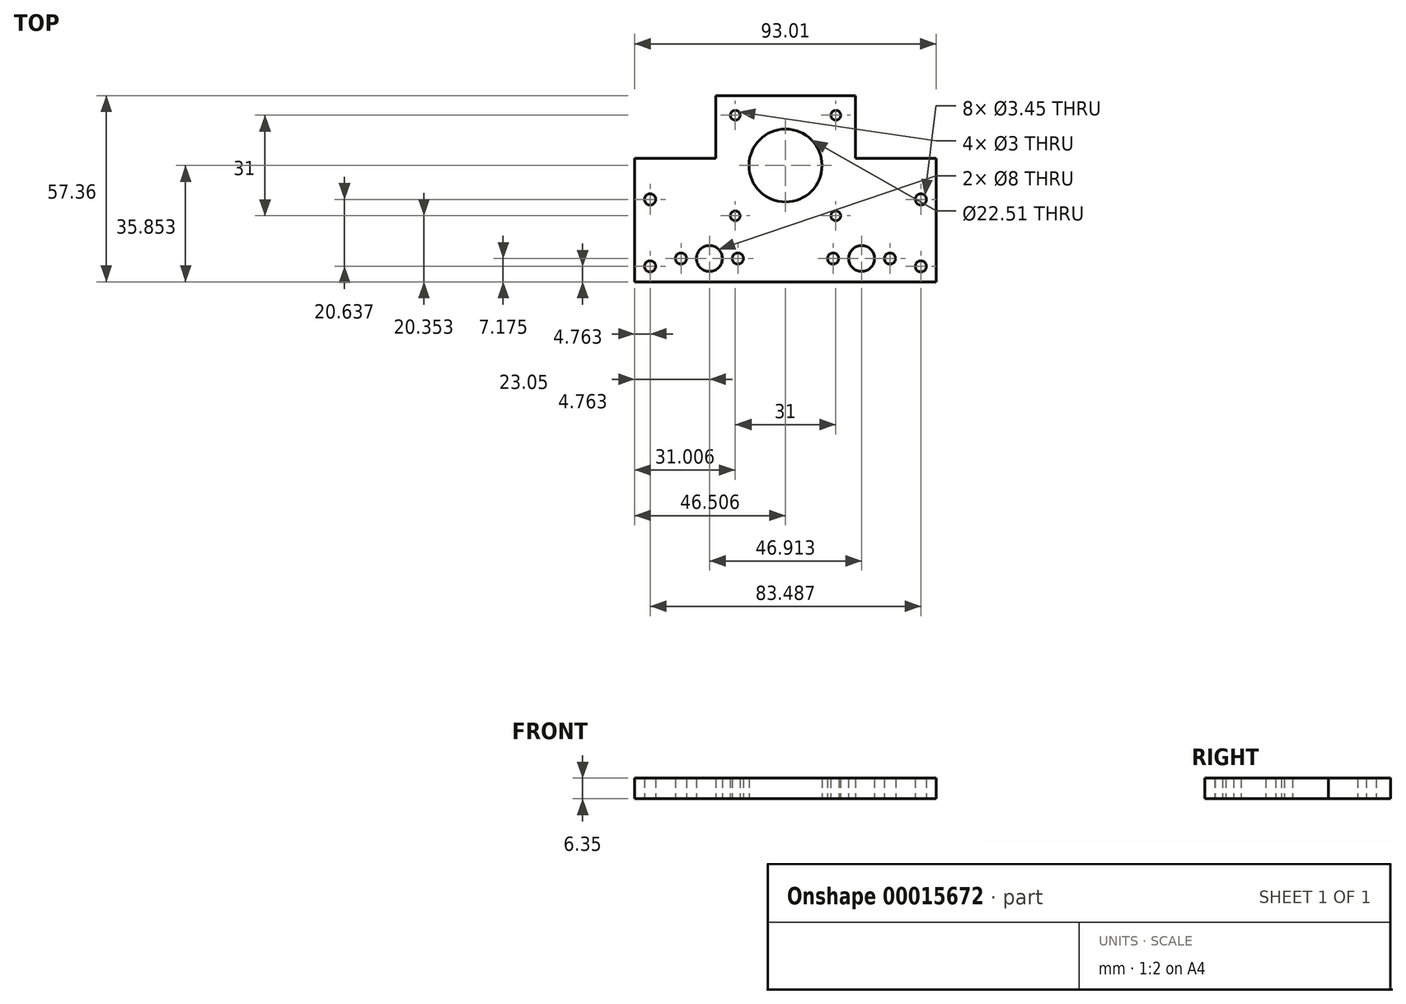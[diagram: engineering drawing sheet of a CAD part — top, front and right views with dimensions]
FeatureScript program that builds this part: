
annotation { "Feature Type Name" : "Feature", "Feature Type Description" : "" }
export const myFeature = defineFeature(function(context is Context, id is Id, definition is map)
    precondition{}
    {
        {
            var Q0;
            Q0=qCreatedBy(makeId("Top.planeOp"),FACE);
            var sketch = newSketch(context, id + "F0", { "sketchPlane" : qUnion([Q0])});
            skLineSegment(sketch, "E0.top", {"start": v(0, -38.1) * mm, "end": v(93.01, -38.1) * mm});
            skLineSegment(sketch, "E0.left", {"start": v(0, 0) * mm, "end": v(0, -38.1) * mm});
            skLineSegment(sketch, "E0.right", {"start": v(93.01, 0) * mm, "end": v(93.01, -38.1) * mm});
            skLineSegment(sketch, "E1", {"start": v(23.05, 0) * mm, "end": v(23.05, -30.92) * mm, "construction": true});
            skLineSegment(sketch, "E2", {"start": v(69.96, 0) * mm, "end": v(69.96, -30.92) * mm, "construction": true});
            skLineSegment(sketch, "E3", {"start": v(61.2, -30.92) * mm, "end": v(78.73, -30.92) * mm, "construction": true});
            skLineSegment(sketch, "E4", {"start": v(14.29, -30.92) * mm, "end": v(31.81, -30.92) * mm, "construction": true});
            skCircle(sketch, "E5", {"center": v(14.29, -30.92) * mm, "radius": 1.73 * mm});
            skCircle(sketch, "E6", {"center": v(23.05, -30.92) * mm, "radius": 4 * mm});
            skCircle(sketch, "E7", {"center": v(31.81, -30.92) * mm, "radius": 1.73 * mm});
            skCircle(sketch, "E8", {"center": v(61.2, -30.92) * mm, "radius": 1.73 * mm});
            skCircle(sketch, "E9", {"center": v(78.73, -30.92) * mm, "radius": 1.73 * mm});
            skCircle(sketch, "E10", {"center": v(69.96, -30.92) * mm, "radius": 4 * mm});
            skLineSegment(sketch, "E11", {"start": v(23.05, -30.92) * mm, "end": v(23.05, -38.1) * mm});
            skLineSegment(sketch, "E12", {"start": v(88.25, 0) * mm, "end": v(88.25, -12.7) * mm, "construction": true});
            skLineSegment(sketch, "E13", {"start": v(88.25, -12.7) * mm, "end": v(88.25, -33.34) * mm, "construction": true});
            skLineSegment(sketch, "E14", {"start": v(4.76, -33.34) * mm, "end": v(4.76, -12.7) * mm, "construction": true});
            skLineSegment(sketch, "E15", {"start": v(4.76, -12.7) * mm, "end": v(4.76, 0) * mm, "construction": true});
            skCircle(sketch, "E16", {"center": v(88.25, -33.34) * mm, "radius": 1.73 * mm});
            skCircle(sketch, "E17", {"center": v(88.25, -12.7) * mm, "radius": 1.73 * mm});
            skCircle(sketch, "E18", {"center": v(4.76, -12.7) * mm, "radius": 1.73 * mm});
            skCircle(sketch, "E19", {"center": v(4.76, -33.34) * mm, "radius": 1.73 * mm});
            skLineSegment(sketch, "E20", {"start": v(78.73, -30.92) * mm, "end": v(88.25, -30.92) * mm, "construction": true});
            skLineSegment(sketch, "E21", {"start": v(88.25, -30.92) * mm, "end": v(93.01, -30.92) * mm});
            skLineSegment(sketch, "E22", {"start": v(14.29, -30.92) * mm, "end": v(4.76, -30.92) * mm, "construction": true});
            skLineSegment(sketch, "E23", {"start": v(4.76, -30.92) * mm, "end": v(0, -30.92) * mm, "construction": true});
            skLineSegment(sketch, "E24", {"start": v(0, 0) * mm, "end": v(25, 0) * mm});
            skLineSegment(sketch, "E25", {"start": v(93.01, 0) * mm, "end": v(68, 0) * mm});
            skLineSegment(sketch, "E26", {"start": v(68, 0) * mm, "end": v(68, 19.26) * mm});
            skLineSegment(sketch, "E27", {"start": v(68, 19.26) * mm, "end": v(25, 19.26) * mm});
            skLineSegment(sketch, "E28", {"start": v(25, 19.26) * mm, "end": v(25, 0) * mm});
            skLineSegment(sketch, "E29", {"start": v(46.5, 19.26) * mm, "end": v(46.5, -2.25) * mm, "construction": true});
            skLineSegment(sketch, "E30.rect.bottom", {"start": v(62, -17.75) * mm, "end": v(31, -17.75) * mm, "construction": true});
            skLineSegment(sketch, "E30.rect.top", {"start": v(62, 13.25) * mm, "end": v(31, 13.25) * mm, "construction": true});
            skLineSegment(sketch, "E30.rect.left", {"start": v(62, -17.75) * mm, "end": v(62, 13.25) * mm, "construction": true});
            skLineSegment(sketch, "E30.rect.right", {"start": v(31, -17.75) * mm, "end": v(31, 13.25) * mm, "construction": true});
            skPoint(sketch, "E30.rect.middle", {"position": v(46.5, -2.25) * mm});
            skCircle(sketch, "E31", {"center": v(46.5, -2.25) * mm, "radius": 11.25 * mm});
            skCircle(sketch, "E32", {"center": v(62, 13.25) * mm, "radius": 1.5 * mm});
            skCircle(sketch, "E33", {"center": v(62, -17.75) * mm, "radius": 1.5 * mm});
            skCircle(sketch, "E34", {"center": v(31, -17.75) * mm, "radius": 1.5 * mm});
            skCircle(sketch, "E35", {"center": v(31, 13.25) * mm, "radius": 1.5 * mm});
            skLineSegment(sketch, "E36", {"start": v(46.5, -2.25) * mm, "end": v(46.5, -23.75) * mm});
            skLineSegment(sketch, "E37", {"start": v(46.5, -23.75) * mm, "end": v(46.5, -38.1) * mm});
            skSolve(sketch);
        }
        {
            var Q0;
            Q0=qSketchRegion(id+"F0",true);
            extrude(context, id + "F1", {"entities" : qUnion([Q0]), "depth" : 6.35 * mm});
        }
    });
